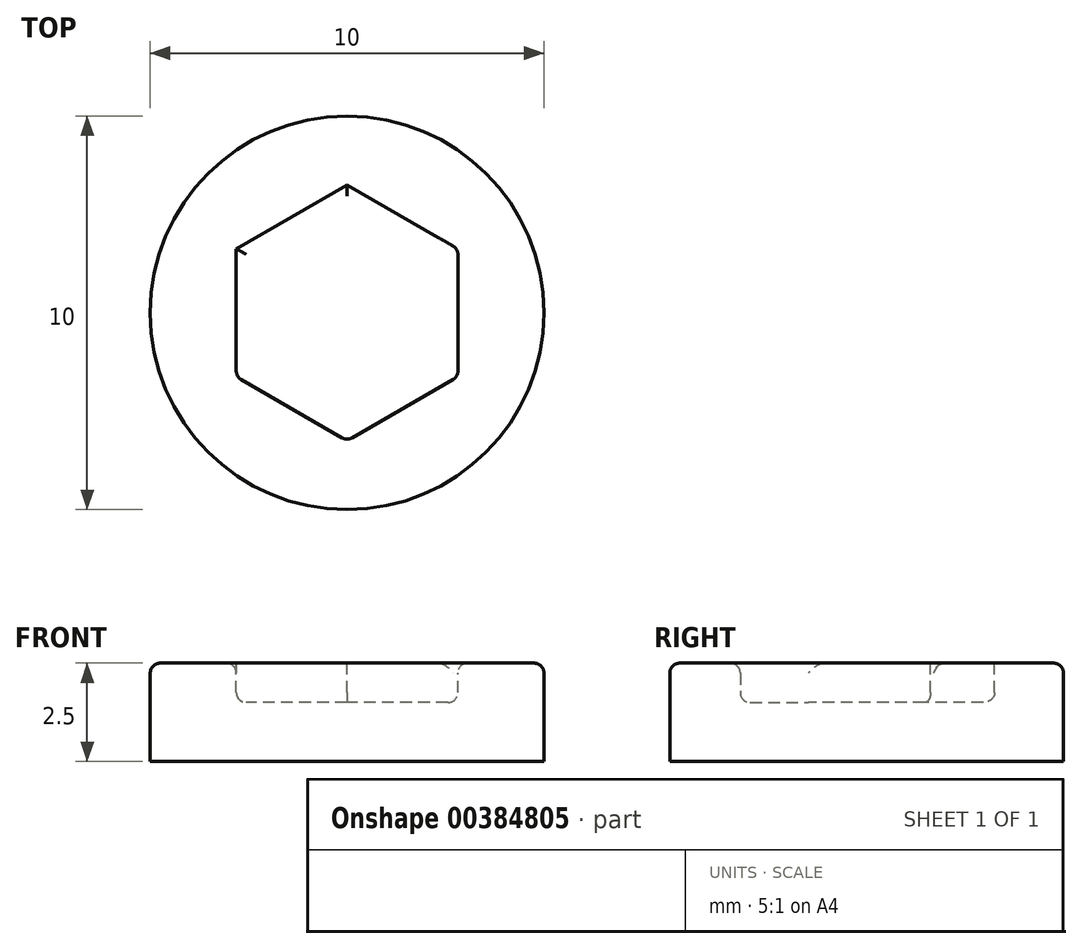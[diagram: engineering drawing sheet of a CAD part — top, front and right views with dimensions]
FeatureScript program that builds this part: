
annotation { "Feature Type Name" : "Feature", "Feature Type Description" : "" }
export const myFeature = defineFeature(function(context is Context, id is Id, definition is map)
    precondition{}
    {
        {
            var Q0;
            Q0=qCreatedBy(makeId("Top.planeOp"),FACE);
            var sketch = newSketch(context, id + "F0", { "sketchPlane" : qUnion([Q0])});
            skCircle(sketch, "E0", {"center": v(0, 0) * mm, "radius": 5 * mm});
            skSolve(sketch);
        }
        {
            var Q0;
            Q0 = qSketchRegion(id + "F0", true);
            extrude(context, id + "F1", {"entities" : qUnion([Q0]), "depth" : 2.5 * mm});
        }
        {
            var Q0;
            Q0=makeQuery(id+"F1.opExtrude","CAP_FACE",FACE,{"disambiguationData":[OSD([sQuery(id+"F0.wireOp",EDGE,"E0")])],"isStart":false});
            var sketch = newSketch(context, id + "F2", { "sketchPlane" : qUnion([Q0])});
            skCircle(sketch, "E1.cCircle", {"center": v(0, 0) * mm, "radius": 3.25 * mm, "construction": true});
            skLineSegment(sketch, "E1.0", {"start": v(0, -3.25) * mm, "end": v(-2.81, -1.63) * mm});
            skLineSegment(sketch, "E1.1", {"start": v(-2.81, -1.62) * mm, "end": v(-2.81, 1.62) * mm});
            skLineSegment(sketch, "E1.2", {"start": v(-2.81, 1.63) * mm, "end": v(0, 3.25) * mm});
            skLineSegment(sketch, "E1.3", {"start": v(0, 3.25) * mm, "end": v(2.81, 1.63) * mm});
            skLineSegment(sketch, "E1.4", {"start": v(2.81, 1.62) * mm, "end": v(2.81, -1.62) * mm});
            skLineSegment(sketch, "E1.5", {"start": v(2.81, -1.62) * mm, "end": v(0, -3.25) * mm});
            skSolve(sketch);
        }
        {
            var Q0;
            Q0=makeQuery(id+"F2.imprint","IMPRINT",FACE,{"disambiguationData":[TD([[makeQuery(id+"F2.imprint","IMPRINT",EDGE,{"derivedFrom":sQuery(id+"F2.wireOp",EDGE,"E1.0")}),-1.0]])]});
            extrude(context, id + "F3", {"entities" : qUnion([Q0]), "operationType" : NewBodyOperationType.REMOVE, "oppositeDirection" : true, "depth" : 1 * mm});
        }
        {
            var Q0;
            Q0=makeQuery(id+"F3.boolean.opBoolean","COPY",FACE,{"derivedFrom":makeQuery(id+"F3.opExtrude","CAP_FACE",FACE,{"disambiguationData":[OSD([sQuery(id+"F2.wireOp",EDGE,"E1.0"),sQuery(id+"F2.wireOp",EDGE,"E1.1"),sQuery(id+"F2.wireOp",EDGE,"E1.2"),sQuery(id+"F2.wireOp",EDGE,"E1.3"),sQuery(id+"F2.wireOp",EDGE,"E1.4"),sQuery(id+"F2.wireOp",EDGE,"E1.5")])],"isStart":false})});
            var Q1;
            Q1=makeQuery(id+"F3.boolean.opBoolean","COPY",FACE,{"derivedFrom":makeQuery(id+"F3.opExtrude","SWEPT_FACE",FACE,{"disambiguationData":[OSD([sQuery(id+"F2.wireOp",EDGE,"E1.4")])]})});
            var Q2;
            Q2=makeQuery(id+"F3.boolean.opBoolean","COPY",EDGE,{"derivedFrom":makeQuery(id+"F3.opExtrude","CAP_EDGE",EDGE,{"disambiguationData":[OSD([sQuery(id+"F2.wireOp",EDGE,"E1.2")])],"isStart":true})});
            var Q3;
            Q3=makeQuery(id+"F3.boolean.opBoolean","COPY",EDGE,{"derivedFrom":makeQuery(id+"F3.opExtrude","CAP_EDGE",EDGE,{"disambiguationData":[OSD([sQuery(id+"F2.wireOp",EDGE,"E1.1")])],"isStart":true})});
            var Q4;
            Q4=makeQuery(id+"F3.boolean.opBoolean","COPY",FACE,{"derivedFrom":makeQuery(id+"F3.opExtrude","SWEPT_FACE",FACE,{"disambiguationData":[OSD([sQuery(id+"F2.wireOp",EDGE,"E1.0")])]})});
            var Q5;
            Q5=makeQuery(id+"F3.boolean.opBoolean","COPY",FACE,{"derivedFrom":makeQuery(id+"F3.opExtrude","SWEPT_FACE",FACE,{"disambiguationData":[OSD([sQuery(id+"F2.wireOp",EDGE,"E1.5")])]})});
            var Q6;
            Q6=makeQuery(id+"F1.opExtrude","CAP_EDGE",EDGE,{"disambiguationData":[OSD([sQuery(id+"F0.wireOp",EDGE,"E0")])],"isStart":false});
            fillet(context, id + "F4", {"entities" : qUnion([Q0, Q1, Q2, Q3, Q4, Q5, Q6]), "radius" : 0.25 * mm, "tangentPropagation" : true, "allowEdgeOverflow" : false});
        }
    });
